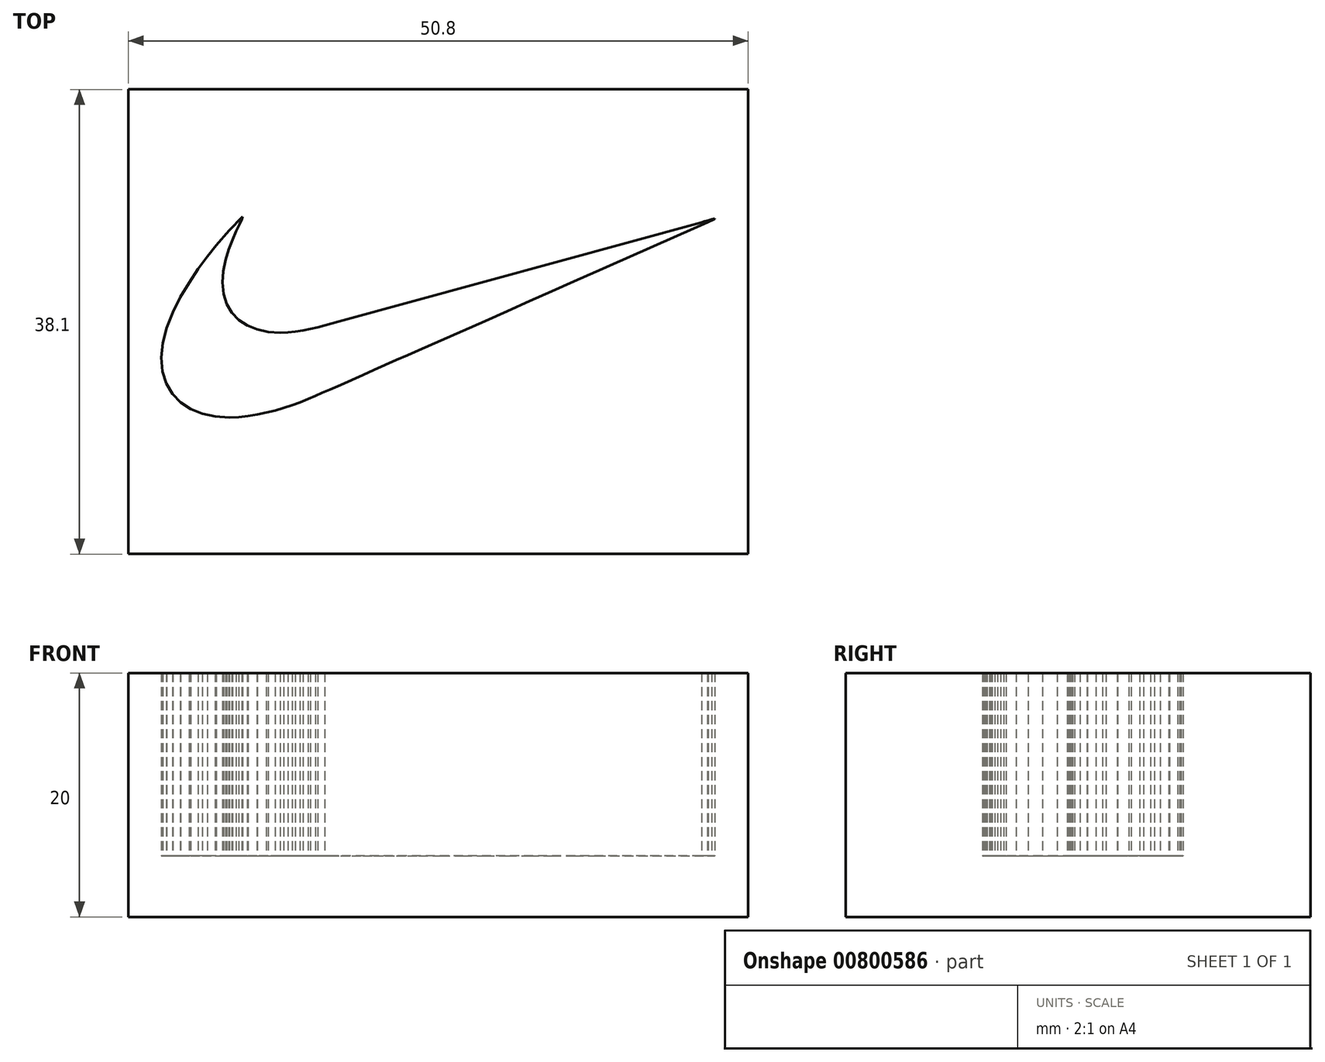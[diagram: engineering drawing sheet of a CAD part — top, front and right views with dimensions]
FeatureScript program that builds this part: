
annotation { "Feature Type Name" : "Feature", "Feature Type Description" : "" }
export const myFeature = defineFeature(function(context is Context, id is Id, definition is map)
    precondition{}
    {
        {
            var Q0;
            Q0=qCreatedBy(makeId("Top.planeOp"),FACE);
            var sketch = newSketch(context, id + "F0", { "sketchPlane" : qUnion([Q0])});
            skLineSegment(sketch, "E0", {"start": v(-22.7, -3.32) * mm, "end": v(-22.59, -4.47) * mm});
            skLineSegment(sketch, "E1", {"start": v(-22.59, -4.47) * mm, "end": v(-22.28, -5.47) * mm});
            skLineSegment(sketch, "E2", {"start": v(-22.28, -5.47) * mm, "end": v(-21.78, -6.31) * mm});
            skLineSegment(sketch, "E3", {"start": v(-21.78, -6.31) * mm, "end": v(-21.11, -7) * mm});
            skLineSegment(sketch, "E4", {"start": v(-21.11, -7) * mm, "end": v(-20.3, -7.54) * mm});
            skLineSegment(sketch, "E5", {"start": v(-20.3, -7.54) * mm, "end": v(-19.34, -7.92) * mm});
            skLineSegment(sketch, "E6", {"start": v(-19.34, -7.92) * mm, "end": v(-18.27, -8.15) * mm});
            skLineSegment(sketch, "E7", {"start": v(-18.27, -8.15) * mm, "end": v(-17.1, -8.23) * mm});
            skLineSegment(sketch, "E8", {"start": v(-17.1, -8.23) * mm, "end": v(-16.34, -8.2) * mm});
            skLineSegment(sketch, "E9", {"start": v(-16.34, -8.2) * mm, "end": v(-15.58, -8.12) * mm});
            skLineSegment(sketch, "E10", {"start": v(-15.58, -8.12) * mm, "end": v(-14.83, -8) * mm});
            skLineSegment(sketch, "E11", {"start": v(-14.83, -8) * mm, "end": v(-14.08, -7.84) * mm});
            skLineSegment(sketch, "E12", {"start": v(-14.08, -7.84) * mm, "end": v(-13.36, -7.66) * mm});
            skLineSegment(sketch, "E13", {"start": v(-13.36, -7.66) * mm, "end": v(-12.65, -7.45) * mm});
            skLineSegment(sketch, "E14", {"start": v(-12.65, -7.45) * mm, "end": v(-11.98, -7.23) * mm});
            skLineSegment(sketch, "E15", {"start": v(-11.98, -7.23) * mm, "end": v(-11.33, -7) * mm});
            skLineSegment(sketch, "E16", {"start": v(-11.33, -7) * mm, "end": v(-10.65, -6.73) * mm});
            skLineSegment(sketch, "E17", {"start": v(-10.65, -6.73) * mm, "end": v(-10.07, -6.48) * mm});
            skLineSegment(sketch, "E18", {"start": v(-10.07, -6.48) * mm, "end": v(-9.5, -6.22) * mm});
            skLineSegment(sketch, "E19", {"start": v(-9.5, -6.22) * mm, "end": v(-8.88, -5.95) * mm});
            skLineSegment(sketch, "E20", {"start": v(-8.88, -5.95) * mm, "end": v(-7.98, -5.57) * mm});
            skLineSegment(sketch, "E21", {"start": v(-7.98, -5.57) * mm, "end": v(-7.08, -5.17) * mm});
            skLineSegment(sketch, "E22", {"start": v(-7.08, -5.17) * mm, "end": v(-6.16, -4.76) * mm});
            skLineSegment(sketch, "E23", {"start": v(-6.16, -4.76) * mm, "end": v(-5.24, -4.35) * mm});
            skLineSegment(sketch, "E24", {"start": v(-5.24, -4.35) * mm, "end": v(-4.33, -3.94) * mm});
            skLineSegment(sketch, "E25", {"start": v(-4.33, -3.94) * mm, "end": v(-3.4, -3.53) * mm});
            skLineSegment(sketch, "E26", {"start": v(-3.4, -3.53) * mm, "end": v(-2.5, -3.12) * mm});
            skLineSegment(sketch, "E27", {"start": v(-2.5, -3.12) * mm, "end": v(-1.6, -2.73) * mm});
            skLineSegment(sketch, "E28", {"start": v(-1.6, -2.73) * mm, "end": v(0.22, -1.93) * mm});
            skLineSegment(sketch, "E29", {"start": v(0.22, -1.93) * mm, "end": v(2.03, -1.13) * mm});
            skLineSegment(sketch, "E30", {"start": v(2.03, -1.13) * mm, "end": v(3.85, -0.33) * mm});
            skLineSegment(sketch, "E31", {"start": v(3.85, -0.33) * mm, "end": v(5.68, 0.49) * mm});
            skLineSegment(sketch, "E32", {"start": v(5.68, 0.49) * mm, "end": v(7.5, 1.3) * mm});
            skLineSegment(sketch, "E33", {"start": v(7.5, 1.3) * mm, "end": v(9.33, 2.11) * mm});
            skLineSegment(sketch, "E34", {"start": v(9.33, 2.11) * mm, "end": v(11.15, 2.92) * mm});
            skLineSegment(sketch, "E35", {"start": v(11.15, 2.92) * mm, "end": v(12.97, 3.73) * mm});
            skLineSegment(sketch, "E36", {"start": v(12.97, 3.73) * mm, "end": v(22.08, 7.76) * mm});
            skLineSegment(sketch, "E37", {"start": v(22.08, 7.76) * mm, "end": v(22.67, 8.04) * mm});
            skLineSegment(sketch, "E38", {"start": v(22.67, 8.04) * mm, "end": v(22.7, 8.06) * mm});
            skLineSegment(sketch, "E39", {"start": v(22.7, 8.06) * mm, "end": v(22.43, 8.01) * mm});
            skLineSegment(sketch, "E40", {"start": v(22.43, 8.01) * mm, "end": v(22.14, 7.93) * mm});
            skLineSegment(sketch, "E41", {"start": v(22.14, 7.93) * mm, "end": v(21.85, 7.84) * mm});
            skLineSegment(sketch, "E42", {"start": v(21.85, 7.84) * mm, "end": v(21.59, 7.77) * mm});
            skLineSegment(sketch, "E43", {"start": v(21.59, 7.77) * mm, "end": v(-8.14, -0.36) * mm});
            skLineSegment(sketch, "E44", {"start": v(-8.14, -0.36) * mm, "end": v(-8.7, -0.52) * mm});
            skLineSegment(sketch, "E45", {"start": v(-8.7, -0.52) * mm, "end": v(-9.29, -0.68) * mm});
            skLineSegment(sketch, "E46", {"start": v(-9.29, -0.68) * mm, "end": v(-9.88, -0.83) * mm});
            skLineSegment(sketch, "E47", {"start": v(-9.88, -0.83) * mm, "end": v(-10.47, -0.98) * mm});
            skLineSegment(sketch, "E48", {"start": v(-10.47, -0.98) * mm, "end": v(-11.08, -1.1) * mm});
            skLineSegment(sketch, "E49", {"start": v(-11.08, -1.1) * mm, "end": v(-11.7, -1.2) * mm});
            skLineSegment(sketch, "E50", {"start": v(-11.7, -1.2) * mm, "end": v(-12.32, -1.26) * mm});
            skLineSegment(sketch, "E51", {"start": v(-12.32, -1.26) * mm, "end": v(-12.95, -1.29) * mm});
            skLineSegment(sketch, "E52", {"start": v(-12.95, -1.29) * mm, "end": v(-13.93, -1.22) * mm});
            skLineSegment(sketch, "E53", {"start": v(-13.93, -1.22) * mm, "end": v(-14.83, -1.02) * mm});
            skLineSegment(sketch, "E54", {"start": v(-14.83, -1.02) * mm, "end": v(-15.64, -0.7) * mm});
            skLineSegment(sketch, "E55", {"start": v(-15.64, -0.7) * mm, "end": v(-16.34, -0.23) * mm});
            skLineSegment(sketch, "E56", {"start": v(-16.34, -0.23) * mm, "end": v(-16.9, 0.35) * mm});
            skLineSegment(sketch, "E57", {"start": v(-16.9, 0.35) * mm, "end": v(-17.33, 1.06) * mm});
            skLineSegment(sketch, "E58", {"start": v(-17.33, 1.06) * mm, "end": v(-17.6, 1.9) * mm});
            skLineSegment(sketch, "E59", {"start": v(-17.6, 1.9) * mm, "end": v(-17.68, 2.85) * mm});
            skLineSegment(sketch, "E60", {"start": v(-17.68, 2.85) * mm, "end": v(-17.61, 3.76) * mm});
            skLineSegment(sketch, "E61", {"start": v(-17.61, 3.76) * mm, "end": v(-17.43, 4.66) * mm});
            skLineSegment(sketch, "E62", {"start": v(-17.43, 4.66) * mm, "end": v(-17.16, 5.53) * mm});
            skLineSegment(sketch, "E63", {"start": v(-17.16, 5.53) * mm, "end": v(-16.86, 6.34) * mm});
            skLineSegment(sketch, "E64", {"start": v(-16.86, 6.34) * mm, "end": v(-16.56, 7.04) * mm});
            skLineSegment(sketch, "E65", {"start": v(-16.56, 7.04) * mm, "end": v(-16.3, 7.61) * mm});
            skLineSegment(sketch, "E66", {"start": v(-16.3, 7.61) * mm, "end": v(-16.1, 8.02) * mm});
            skLineSegment(sketch, "E67", {"start": v(-16.1, 8.02) * mm, "end": v(-16.01, 8.23) * mm});
            skLineSegment(sketch, "E68", {"start": v(-16.01, 8.23) * mm, "end": v(-17.14, 7.1) * mm});
            skLineSegment(sketch, "E69", {"start": v(-17.14, 7.1) * mm, "end": v(-18.2, 5.88) * mm});
            skLineSegment(sketch, "E70", {"start": v(-18.2, 5.88) * mm, "end": v(-18.92, 4.98) * mm});
            skLineSegment(sketch, "E71", {"start": v(-18.92, 4.98) * mm, "end": v(-19.67, 3.95) * mm});
            skLineSegment(sketch, "E72", {"start": v(-19.67, 3.95) * mm, "end": v(-20.42, 2.82) * mm});
            skLineSegment(sketch, "E73", {"start": v(-20.42, 2.82) * mm, "end": v(-21.13, 1.62) * mm});
            skLineSegment(sketch, "E74", {"start": v(-21.13, 1.62) * mm, "end": v(-21.75, 0.38) * mm});
            skLineSegment(sketch, "E75", {"start": v(-21.75, 0.38) * mm, "end": v(-22.25, -0.87) * mm});
            skLineSegment(sketch, "E76", {"start": v(-22.25, -0.87) * mm, "end": v(-22.57, -2.12) * mm});
            skLineSegment(sketch, "E77", {"start": v(-22.57, -2.12) * mm, "end": v(-22.7, -3.32) * mm});
            skLineSegment(sketch, "E78.bottom", {"start": v(-25.4, -19.44) * mm, "end": v(25.4, -19.44) * mm});
            skLineSegment(sketch, "E78.top", {"start": v(-25.4, 18.66) * mm, "end": v(25.4, 18.66) * mm});
            skLineSegment(sketch, "E78.left", {"start": v(-25.4, -19.44) * mm, "end": v(-25.4, 18.66) * mm});
            skLineSegment(sketch, "E78.right", {"start": v(25.4, -19.44) * mm, "end": v(25.4, 18.66) * mm});
            skSolve(sketch);
        }
        {
            var Q0;
            Q0=makeQuery(id+"F0.imprint","IMPRINT",FACE,{"disambiguationData":[TD([[makeQuery(id+"F0.imprint","IMPRINT",EDGE,{"derivedFrom":sQuery(id+"F0.wireOp",EDGE,"E0")}),-1.0]])]});
            extrude(context, id + "F1", {"entities" : qUnion([Q0]), "depth" : 15 * mm, "offsetDistance" : 25.4 * mm});
        }
        {
            var Q0;
            Q0=makeQuery(id+"F1.opExtrude","CAP_FACE",FACE,{"disambiguationData":[OSD([sQuery(id+"F0.wireOp",EDGE,"E0"),sQuery(id+"F0.wireOp",EDGE,"E1"),sQuery(id+"F0.wireOp",EDGE,"E2"),sQuery(id+"F0.wireOp",EDGE,"E3"),sQuery(id+"F0.wireOp",EDGE,"E4"),sQuery(id+"F0.wireOp",EDGE,"E5"),sQuery(id+"F0.wireOp",EDGE,"E6"),sQuery(id+"F0.wireOp",EDGE,"E7"),sQuery(id+"F0.wireOp",EDGE,"E8"),sQuery(id+"F0.wireOp",EDGE,"E9"),sQuery(id+"F0.wireOp",EDGE,"E10"),sQuery(id+"F0.wireOp",EDGE,"E11"),sQuery(id+"F0.wireOp",EDGE,"E12"),sQuery(id+"F0.wireOp",EDGE,"E13"),sQuery(id+"F0.wireOp",EDGE,"E14"),sQuery(id+"F0.wireOp",EDGE,"E15"),sQuery(id+"F0.wireOp",EDGE,"E16"),sQuery(id+"F0.wireOp",EDGE,"E17"),sQuery(id+"F0.wireOp",EDGE,"E18"),sQuery(id+"F0.wireOp",EDGE,"E19"),sQuery(id+"F0.wireOp",EDGE,"E20"),sQuery(id+"F0.wireOp",EDGE,"E21"),sQuery(id+"F0.wireOp",EDGE,"E22"),sQuery(id+"F0.wireOp",EDGE,"E23"),sQuery(id+"F0.wireOp",EDGE,"E24"),sQuery(id+"F0.wireOp",EDGE,"E25"),sQuery(id+"F0.wireOp",EDGE,"E26"),sQuery(id+"F0.wireOp",EDGE,"E27"),sQuery(id+"F0.wireOp",EDGE,"E28"),sQuery(id+"F0.wireOp",EDGE,"E29"),sQuery(id+"F0.wireOp",EDGE,"E30"),sQuery(id+"F0.wireOp",EDGE,"E31"),sQuery(id+"F0.wireOp",EDGE,"E32"),sQuery(id+"F0.wireOp",EDGE,"E33"),sQuery(id+"F0.wireOp",EDGE,"E34"),sQuery(id+"F0.wireOp",EDGE,"E35"),sQuery(id+"F0.wireOp",EDGE,"E36"),sQuery(id+"F0.wireOp",EDGE,"E37"),sQuery(id+"F0.wireOp",EDGE,"E38"),sQuery(id+"F0.wireOp",EDGE,"E39"),sQuery(id+"F0.wireOp",EDGE,"E40"),sQuery(id+"F0.wireOp",EDGE,"E41"),sQuery(id+"F0.wireOp",EDGE,"E42"),sQuery(id+"F0.wireOp",EDGE,"E43"),sQuery(id+"F0.wireOp",EDGE,"E44"),sQuery(id+"F0.wireOp",EDGE,"E45"),sQuery(id+"F0.wireOp",EDGE,"E46"),sQuery(id+"F0.wireOp",EDGE,"E47"),sQuery(id+"F0.wireOp",EDGE,"E48"),sQuery(id+"F0.wireOp",EDGE,"E49"),sQuery(id+"F0.wireOp",EDGE,"E50"),sQuery(id+"F0.wireOp",EDGE,"E51"),sQuery(id+"F0.wireOp",EDGE,"E52"),sQuery(id+"F0.wireOp",EDGE,"E53"),sQuery(id+"F0.wireOp",EDGE,"E54"),sQuery(id+"F0.wireOp",EDGE,"E55"),sQuery(id+"F0.wireOp",EDGE,"E56"),sQuery(id+"F0.wireOp",EDGE,"E57"),sQuery(id+"F0.wireOp",EDGE,"E58"),sQuery(id+"F0.wireOp",EDGE,"E59"),sQuery(id+"F0.wireOp",EDGE,"E60"),sQuery(id+"F0.wireOp",EDGE,"E61"),sQuery(id+"F0.wireOp",EDGE,"E62"),sQuery(id+"F0.wireOp",EDGE,"E63"),sQuery(id+"F0.wireOp",EDGE,"E64"),sQuery(id+"F0.wireOp",EDGE,"E65"),sQuery(id+"F0.wireOp",EDGE,"E66"),sQuery(id+"F0.wireOp",EDGE,"E67"),sQuery(id+"F0.wireOp",EDGE,"E68"),sQuery(id+"F0.wireOp",EDGE,"E69"),sQuery(id+"F0.wireOp",EDGE,"E70"),sQuery(id+"F0.wireOp",EDGE,"E71"),sQuery(id+"F0.wireOp",EDGE,"E72"),sQuery(id+"F0.wireOp",EDGE,"E73"),sQuery(id+"F0.wireOp",EDGE,"E74"),sQuery(id+"F0.wireOp",EDGE,"E75"),sQuery(id+"F0.wireOp",EDGE,"E76"),sQuery(id+"F0.wireOp",EDGE,"E77"),sQuery(id+"F0.wireOp",EDGE,"E78.bottom"),sQuery(id+"F0.wireOp",EDGE,"E78.top"),sQuery(id+"F0.wireOp",EDGE,"E78.left"),sQuery(id+"F0.wireOp",EDGE,"E78.right")])],"isStart":true});
            var sketch = newSketch(context, id + "F2", { "sketchPlane" : qUnion([Q0])});
            skLineSegment(sketch, "E79.bottom", {"start": v(-25.4, 19.44) * mm, "end": v(25.4, 19.44) * mm});
            skLineSegment(sketch, "E79.top", {"start": v(-25.4, -18.66) * mm, "end": v(25.4, -18.66) * mm});
            skLineSegment(sketch, "E79.left", {"start": v(-25.4, 19.44) * mm, "end": v(-25.4, -18.66) * mm});
            skLineSegment(sketch, "E79.right", {"start": v(25.4, 19.44) * mm, "end": v(25.4, -18.66) * mm});
            skSolve(sketch);
        }
        {
            var Q0;
            Q0 = qSketchRegion(id + "F2", true);
            extrude(context, id + "F3", {"entities" : qUnion([Q0]), "operationType" : NewBodyOperationType.ADD, "depth" : 5 * mm, "offsetDistance" : 25.4 * mm});
        }
    });
